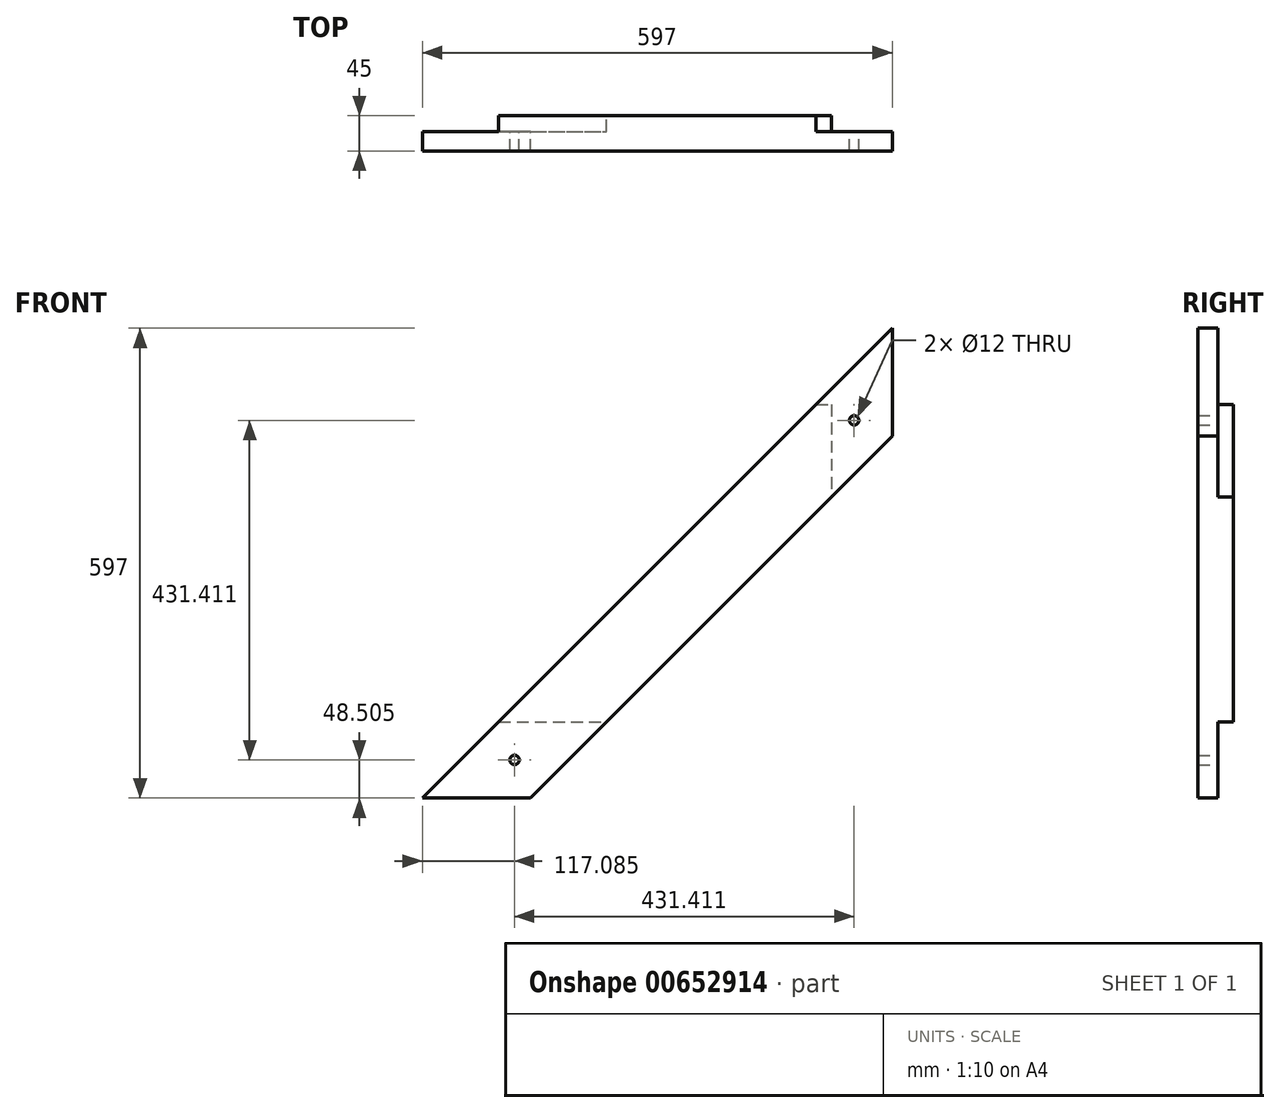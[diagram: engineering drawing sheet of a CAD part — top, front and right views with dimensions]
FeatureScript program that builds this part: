
annotation { "Feature Type Name" : "Feature", "Feature Type Description" : "" }
export const myFeature = defineFeature(function(context is Context, id is Id, definition is map)
    precondition{}
    {
        {
            var Q0;
            Q0=qCreatedBy(makeId("Front.planeOp"),FACE);
            var sketch = newSketch(context, id + "F0", { "sketchPlane" : qUnion([Q0])});
            skLineSegment(sketch, "E0", {"start": v(264.2, 332.8) * mm, "end": v(-332.8, -264.2) * mm});
            skLineSegment(sketch, "E1", {"start": v(264.2, 332.8) * mm, "end": v(264.2, 195.62) * mm});
            skLineSegment(sketch, "E2", {"start": v(-195.62, -264.2) * mm, "end": v(264.2, 195.62) * mm});
            skLineSegment(sketch, "E3", {"start": v(-195.62, -264.2) * mm, "end": v(-332.8, -264.2) * mm});
            skLineSegment(sketch, "E4", {"start": v(-34.3, 34.3) * mm, "end": v(0, 0) * mm, "construction": true});
            skLineSegment(sketch, "E5", {"start": v(0, 0) * mm, "end": v(264.2, 264.2) * mm, "construction": true});
            skLineSegment(sketch, "E6", {"start": v(-235.8, -167.2) * mm, "end": v(-98.62, -167.2) * mm, "construction": true});
            skLineSegment(sketch, "E7", {"start": v(167.2, 235.8) * mm, "end": v(167.2, 98.62) * mm, "construction": true});
            skLineSegment(sketch, "E8", {"start": v(-98.62, -167.2) * mm, "end": v(167.2, -167.2) * mm, "construction": true});
            skLineSegment(sketch, "E9", {"start": v(167.2, -167.2) * mm, "end": v(167.2, 98.62) * mm, "construction": true});
            skSolve(sketch);
        }
        {
            var Q0;
            Q0 = qSketchRegion(id + "F0", true);
            extrude(context, id + "F1", {"entities" : qUnion([Q0]), "endBound" : BoundingType.SYMMETRIC, "depth" : 45 * mm, "offsetDistance" : 25 * mm});
        }
        {
            var Q0;
            Q0=makeQuery(id+"F1.opExtrude","CAP_FACE",FACE,{"disambiguationData":[OSD([sQuery(id+"F0.wireOp",EDGE,"E0"),sQuery(id+"F0.wireOp",EDGE,"E1"),sQuery(id+"F0.wireOp",EDGE,"E2"),sQuery(id+"F0.wireOp",EDGE,"E3")])],"isStart":true});
            var sketch = newSketch(context, id + "F2", { "sketchPlane" : qUnion([Q0])});
            skLineSegment(sketch, "E10", {"start": v(-167.2, 235.8) * mm, "end": v(-187.2, 235.8) * mm});
            skLineSegment(sketch, "E11", {"start": v(-187.2, 235.8) * mm, "end": v(-187.2, 118.62) * mm});
            skLineSegment(sketch, "E12", {"start": v(-167.2, 235.8) * mm, "end": v(-264.2, 332.8) * mm});
            skLineSegment(sketch, "E13", {"start": v(-264.2, 332.8) * mm, "end": v(-264.2, 195.62) * mm});
            skLineSegment(sketch, "E14", {"start": v(-264.2, 195.62) * mm, "end": v(-187.2, 118.62) * mm});
            skSolve(sketch);
        }
        {
            var Q0;
            Q0 = qSketchRegion(id + "F2", true);
            extrude(context, id + "F3", {"entities" : qUnion([Q0]), "operationType" : NewBodyOperationType.REMOVE, "oppositeDirection" : true, "depth" : (45 - 25) * mm, "offsetDistance" : 25 * mm});
        }
        {
            var Q0;
            Q0=makeQuery(id+"F1.opExtrude","CAP_FACE",FACE,{"disambiguationData":[OSD([sQuery(id+"F0.wireOp",EDGE,"E0"),sQuery(id+"F0.wireOp",EDGE,"E1"),sQuery(id+"F0.wireOp",EDGE,"E2"),sQuery(id+"F0.wireOp",EDGE,"E3")])],"isStart":true});
            var sketch = newSketch(context, id + "F4", { "sketchPlane" : qUnion([Q0])});
            skLineSegment(sketch, "E15", {"start": v(235.8, -167.2) * mm, "end": v(98.62, -167.2) * mm});
            skLineSegment(sketch, "E16", {"start": v(98.62, -167.2) * mm, "end": v(195.62, -264.2) * mm});
            skLineSegment(sketch, "E17", {"start": v(195.62, -264.2) * mm, "end": v(332.8, -264.2) * mm});
            skLineSegment(sketch, "E18", {"start": v(332.8, -264.2) * mm, "end": v(235.8, -167.2) * mm});
            skSolve(sketch);
        }
        {
            var Q0;
            Q0 = qSketchRegion(id + "F4", true);
            extrude(context, id + "F5", {"entities" : qUnion([Q0]), "operationType" : NewBodyOperationType.REMOVE, "oppositeDirection" : true, "depth" : 20 * mm, "offsetDistance" : 25 * mm});
        }
        {
            var Q0;
            Q0=makeQuery(id+"F3.boolean.opBoolean","COPY",FACE,{"derivedFrom":makeQuery(id+"F3.opExtrude","CAP_FACE",FACE,{"disambiguationData":[OSD([sQuery(id+"F2.wireOp",EDGE,"E10"),sQuery(id+"F2.wireOp",EDGE,"E11"),sQuery(id+"F2.wireOp",EDGE,"E12"),sQuery(id+"F2.wireOp",EDGE,"E13"),sQuery(id+"F2.wireOp",EDGE,"E14")])],"isStart":false})});
            var sketch = newSketch(context, id + "F6", { "sketchPlane" : qUnion([Q0])});
            skLineSegment(sketch, "E19", {"start": v(-215.7, 284.3) * mm, "end": v(-215.7, 147.12) * mm, "construction": true});
            skCircle(sketch, "E20", {"center": v(-215.7, 215.7) * mm, "radius": 6 * mm});
            skSolve(sketch);
        }
        {
            var Q0;
            Q0 = qSketchRegion(id + "F6", true);
            extrude(context, id + "F7", {"entities" : qUnion([Q0]), "operationType" : NewBodyOperationType.REMOVE, "endBound" : BoundingType.UP_TO_NEXT, "oppositeDirection" : true, "depth" : 25 * mm, "offsetDistance" : 25 * mm});
        }
        {
            var Q0;
            Q0=makeQuery(id+"F5.boolean.opBoolean","COPY",FACE,{"derivedFrom":makeQuery(id+"F5.opExtrude","CAP_FACE",FACE,{"disambiguationData":[OSD([sQuery(id+"F4.wireOp",EDGE,"E15"),sQuery(id+"F4.wireOp",EDGE,"E16"),sQuery(id+"F4.wireOp",EDGE,"E17"),sQuery(id+"F4.wireOp",EDGE,"E18")])],"isStart":false})});
            var sketch = newSketch(context, id + "F8", { "sketchPlane" : qUnion([Q0])});
            skLineSegment(sketch, "E21", {"start": v(284.3, -215.7) * mm, "end": v(147.12, -215.7) * mm, "construction": true});
            skCircle(sketch, "E22", {"center": v(215.7, -215.7) * mm, "radius": 6 * mm});
            skSolve(sketch);
        }
        {
            var Q0;
            Q0 = qSketchRegion(id + "F8", true);
            extrude(context, id + "F9", {"entities" : qUnion([Q0]), "operationType" : NewBodyOperationType.REMOVE, "endBound" : BoundingType.UP_TO_NEXT, "oppositeDirection" : true, "depth" : 25 * mm, "offsetDistance" : 25 * mm});
        }
    });
